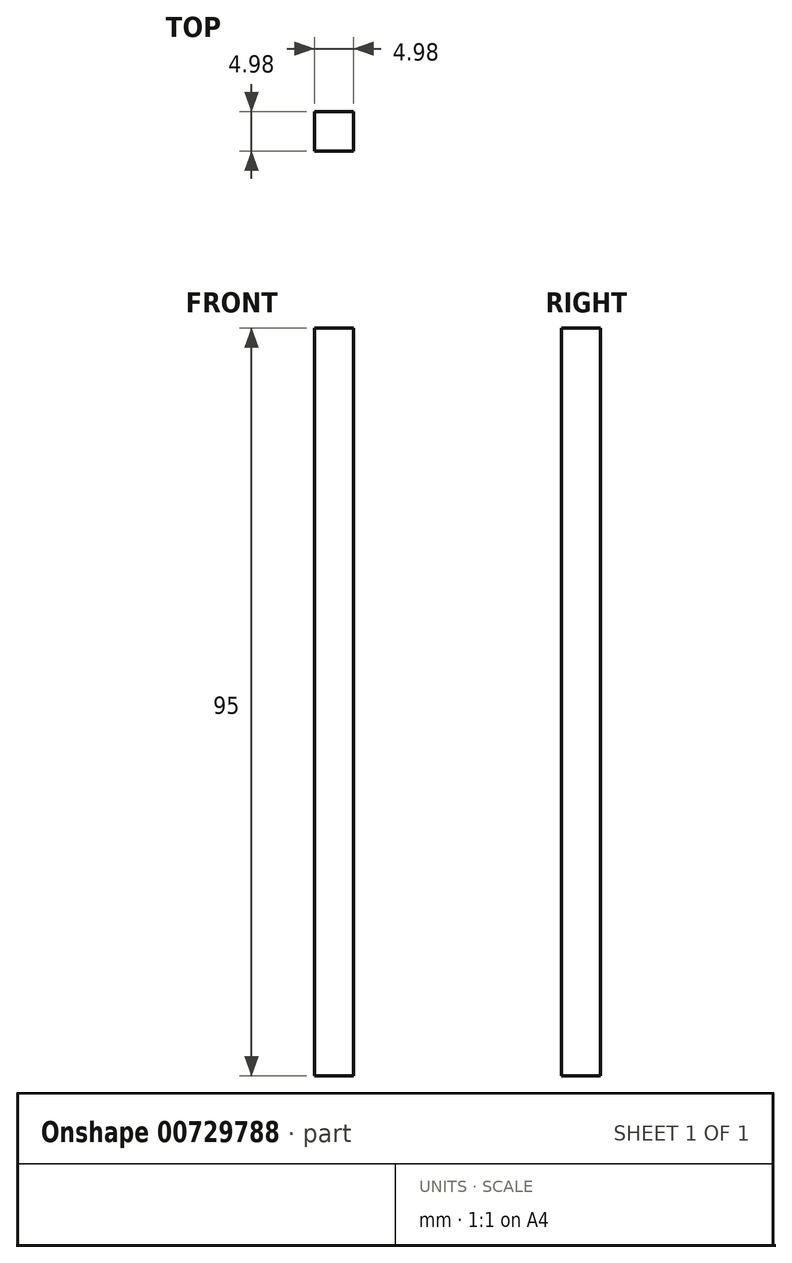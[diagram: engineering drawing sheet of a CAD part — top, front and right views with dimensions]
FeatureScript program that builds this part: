
annotation { "Feature Type Name" : "Feature", "Feature Type Description" : "" }
export const myFeature = defineFeature(function(context is Context, id is Id, definition is map)
    precondition{}
    {
        {
            var Q0;
            Q0=qCreatedBy(makeId("Top.planeOp"),FACE);
            var sketch = newSketch(context, id + "F0", { "sketchPlane" : qUnion([Q0])});
            skLineSegment(sketch, "E0.bottom", {"start": v(-6.87, 32.6) * mm, "end": v(-1.9, 32.6) * mm});
            skLineSegment(sketch, "E0.top", {"start": v(-6.87, 27.61) * mm, "end": v(-1.9, 27.61) * mm});
            skLineSegment(sketch, "E0.left", {"start": v(-6.87, 32.6) * mm, "end": v(-6.87, 27.61) * mm});
            skLineSegment(sketch, "E0.right", {"start": v(-1.9, 32.6) * mm, "end": v(-1.9, 27.61) * mm});
            skSolve(sketch);
        }
        {
            var Q0;
            Q0 = qSketchRegion(id + "F0", true);
            extrude(context, id + "F1", {"entities" : qUnion([Q0]), "depth" : 95 * mm, "offsetDistance" : 25 * mm});
        }
    });
